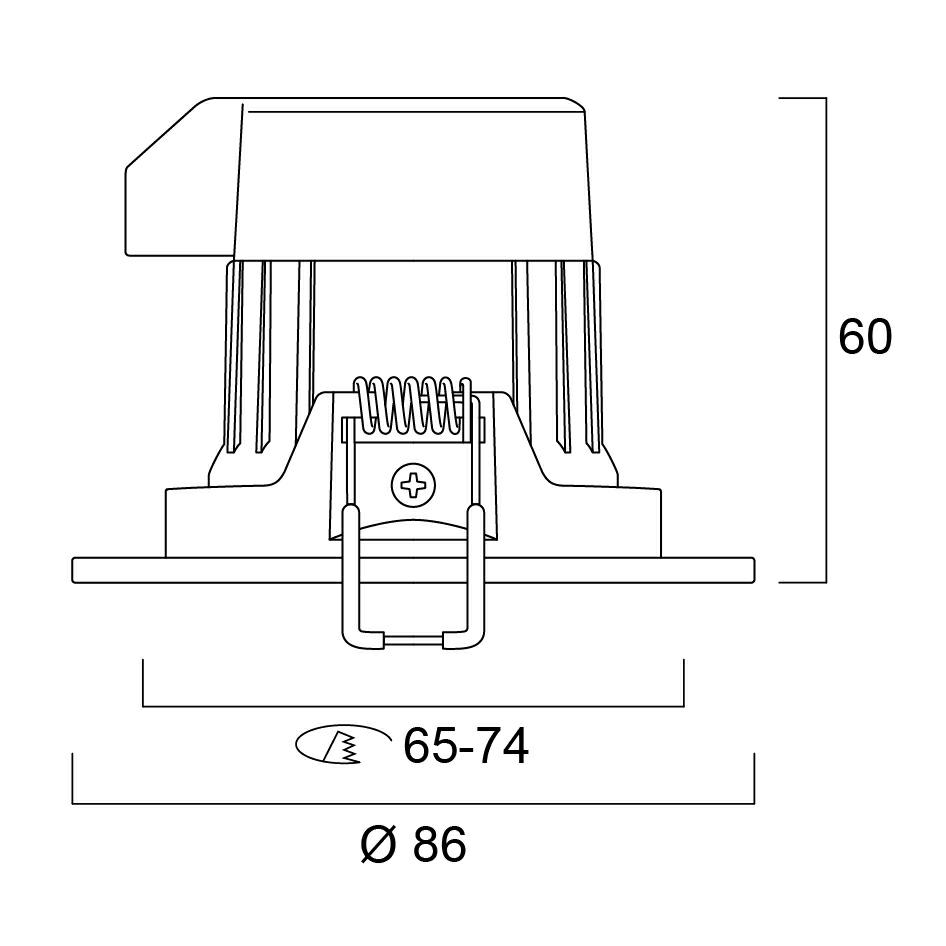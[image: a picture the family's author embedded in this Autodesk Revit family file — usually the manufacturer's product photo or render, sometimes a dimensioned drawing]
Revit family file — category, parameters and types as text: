
# Revit family: 5187
name_source: partatom
category: Lighting Fixtures
revit_build: Autodesk Revit 2018 (Build: 20170223_1515(x64)
units: mm (PartAtom-declared; Revit-internal decimal feet)

## family parameters
Cut with Voids When Loaded = No
Host = Face
Light Source = No
OmniClass Number = 23.80.70.00
OmniClass Title = Lighting
Part Type = Normal
Room Calculation Point = No
Round Connector Dimension = Use Diameter
Shared = No

## types (1)
- 0005187 START SPOT ALU 870LM 3CCT DIM IP65 WHT
    Apparent Load = 9 VA
    Assembly Code = D5020200
    AssetType = Fixed
    ClassificationName = Uniclass2015
    ClassificationValue = EF_70_80
    Cost = 0 $
    Default Elevation = 1219 mm
    DepthDiffuser_FEILO = 5 mm  [stored 0.0164042 ft]
    Description = Integrated LED recessed spotlight, white bezel colour, white reflector, 50° degree beam angle, polycarbonate and aluminium body, low profile 68.5mm recessed depth, IP65 from the front, IK03, loop-in/loop-out terminals for fast wiring,85mm bezel diameter, 68mm cutout, clear lens.
    DiameterBezel_FEILO = 86 mm  [stored 0.282152 ft]
    DocumentationLiterature = http://www.sylvania-lighting.com
    DurationUnit = hours
    ElectricShockClassification = 100
    ExpectedLife = 50000
    HeightBezel_FEILO = 2 mm  [stored 0.00656168 ft]
    IfcExportAs = Class II
    IfcExportType = IfcLightFixtureType
    ImpactProtectionIndex = IfcLightFixtureType
    IngressProtection = IfcLightFixtureType
    InputNominalFrequency = 3000
    InputVoltage = 0
    LampColourRenderingIndex = 16500
    LampColourTemperature = LED
    LampMacAdamStep = 80
    LampNominalLuminous = 3000 K
    LightOutputRatio = LED
    LuminaireType = 0
    ManufacturerName = 100 lm/W
    Material = Feilo Sylvania
    Material_1_FEILO = Body-Sylvania-StartSpot-White
    Material_2_FEILO = LED-Sylvania-StartSpot
    Material_3_FEILO = <By Category>
    Material_4_FEILO = <By Category>
    Model = START SPOT ALU 870LM 3CCT DIM IP65 WHT
    ModelNumber = 0005187
    ModelReference = START SPOT ALU 870LM 3CCT DIM IP65 WHT
    Name = START SPOT ALU 870LM 3CCT DIM IP65 WHT
    NominalDepth = 86 mm  [stored 0.282152 ft]
    NominalHeight = 60 mm  [stored 0.19685 ft]
    NominalLength = 86 mm  [stored 0.282152 ft]
    PowerConsumption = Lighting
    PowerFactor = 0
    RadiusCutout_FEILO = 36 mm
    RadiusDiffuser_FEILO = 14 mm  [stored 0.0459318 ft]
    RadiusOptics_FEILO = 99 mm
    Type Image = <None>
    TypeHead_FEILO = Start Spot IP20 Head : 0005184 START SPOT ALU 870LM 3CCT DIM IP44 WHT
    TypeName = START SPOT ALU 870LM 3CCT DIM IP65 WHT
    URL = 0.9
    VisibilityTop_FEILO = Yes
    Voltage = 230 V
    WarrantyDescription = http://www.sylvania-lighting.com

note: [stored X ft] marks values corroborated as IEEE doubles in the binary element streams (Revit-internal decimal feet)

## geometry (parser evidence)
native form markers: Sweep x8
no freeform markers — native parametric forms only
